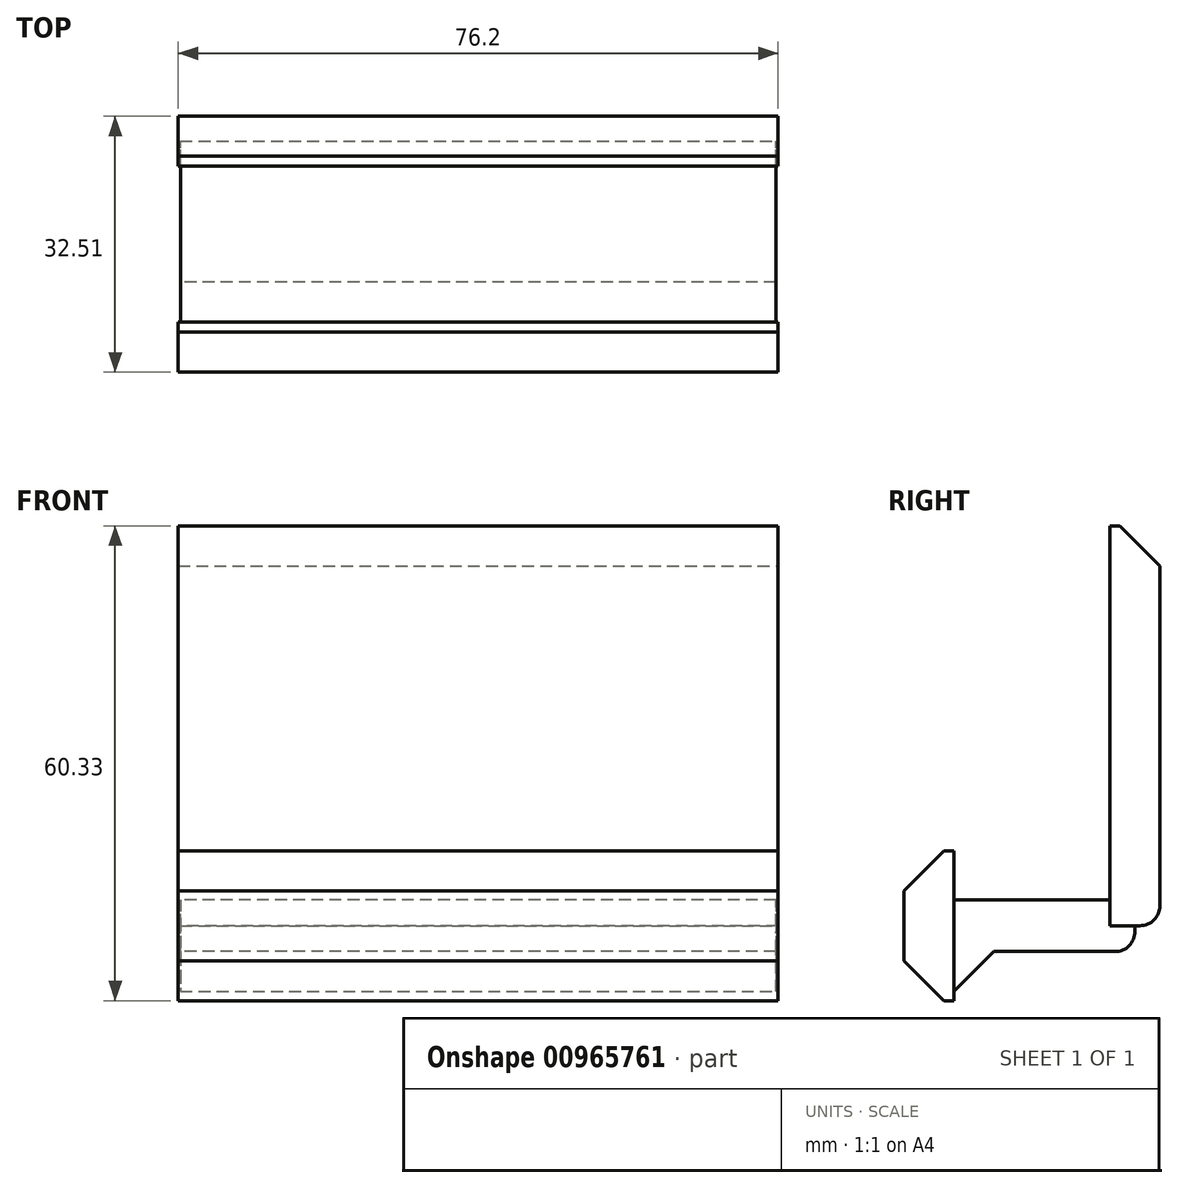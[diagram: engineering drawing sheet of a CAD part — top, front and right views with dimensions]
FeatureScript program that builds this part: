
annotation { "Feature Type Name" : "Feature", "Feature Type Description" : "" }
export const myFeature = defineFeature(function(context is Context, id is Id, definition is map)
    precondition{}
    {
        {
            var Q0;
            Q0=qCreatedBy(makeId("Top.planeOp"),FACE);
            var sketch = newSketch(context, id + "F0", { "sketchPlane" : qUnion([Q0])});
            skLineSegment(sketch, "E0.bottom", {"start": v(38.1, 3.18) * mm, "end": v(-38.1, 3.18) * mm});
            skLineSegment(sketch, "E0.top", {"start": v(38.1, -3.18) * mm, "end": v(-38.1, -3.18) * mm});
            skLineSegment(sketch, "E0.left", {"start": v(38.1, 3.18) * mm, "end": v(38.1, -3.18) * mm});
            skLineSegment(sketch, "E0.right", {"start": v(-38.1, 3.18) * mm, "end": v(-38.1, -3.18) * mm});
            skPoint(sketch, "E0.middle", {"position": v(0, 0) * mm});
            skSolve(sketch);
        }
        {
            var Q0;
            Q0=makeQuery(id+"F0.imprint","IMPRINT",FACE,{"disambiguationData":[TD([[makeQuery(id+"F0.imprint","IMPRINT",EDGE,{"derivedFrom":sQuery(id+"F0.wireOp",EDGE,"E0.bottom")}),1.0]])]});
            extrude(context, id + "F1", {"entities" : qUnion([Q0]), "depth" : 50.8 * mm, "offsetDistance" : 25.4 * mm});
        }
        {
            var Q0;
            Q0=qCreatedBy(makeId("Front.planeOp"),FACE);
            var sketch = newSketch(context, id + "F2", { "sketchPlane" : qUnion([Q0])});
            skLineSegment(sketch, "E1.bottom", {"start": v(37.8, 3.3) * mm, "end": v(-37.8, 3.3) * mm});
            skLineSegment(sketch, "E1.top", {"start": v(37.8, -3.3) * mm, "end": v(-37.8, -3.3) * mm});
            skLineSegment(sketch, "E1.left", {"start": v(37.8, 3.3) * mm, "end": v(37.8, -3.3) * mm});
            skLineSegment(sketch, "E1.right", {"start": v(-37.8, 3.3) * mm, "end": v(-37.8, -3.3) * mm});
            skPoint(sketch, "E1.middle", {"position": v(0, 0) * mm});
            skSolve(sketch);
        }
        {
            var Q0;
            Q0=makeQuery(id+"F2.imprint","IMPRINT",FACE,{"disambiguationData":[TD([[makeQuery(id+"F2.imprint","IMPRINT",EDGE,{"derivedFrom":sQuery(id+"F2.wireOp",EDGE,"E1.bottom")}),1.0]])]});
            extrude(context, id + "F3", {"entities" : qUnion([Q0]), "operationType" : NewBodyOperationType.ADD, "depth" : 25.4 * mm, "offsetDistance" : 25.4 * mm});
        }
        {
            var Q0;
            Q0=makeQuery(id+"F3.opExtrude","CAP_EDGE",EDGE,{"disambiguationData":[OSD([sQuery(id+"F2.wireOp",EDGE,"E1.top")])],"isStart":true});
            var Q1;
            Q1=makeQuery(id+"F1.opExtrude","CAP_EDGE",EDGE,{"disambiguationData":[OSD([sQuery(id+"F0.wireOp",EDGE,"E0.bottom")])],"isStart":true});
            fillet(context, id + "F4", {"entities" : qUnion([Q0, Q1]), "radius" : 2.54 * mm, "tangentPropagation" : true, "allowEdgeOverflow" : false});
        }
        {
            var Q0;
            Q0=makeQuery(id+"F1.opExtrude","CAP_EDGE",EDGE,{"disambiguationData":[OSD([sQuery(id+"F0.wireOp",EDGE,"E0.bottom")])],"isStart":false});
            chamfer(context, id + "F5", {"entities" : qUnion([Q0]), "width" : 5.08 * mm, "tangentPropagation" : true});
        }
        {
            var Q0;
            Q0=makeQuery(id+"F1.opExtrude","SWEPT_BODY",BODY,{"disambiguationData":[OSD([sQuery(id+"F0.wireOp",EDGE,"E0.bottom"),sQuery(id+"F0.wireOp",EDGE,"E0.top"),sQuery(id+"F0.wireOp",EDGE,"E0.left"),sQuery(id+"F0.wireOp",EDGE,"E0.right")])]});
            transform(context, id + "F6", {"entities" : qUnion([Q0]), "transformType" : TransformType.TRANSLATION_3D, "dx" : 0 * mm, "dy" : 26.16 * mm, "dz" : 0 * mm, "makeCopy" : false});
        }
        {
            var Q0;
            Q0 = qSketchRegion(id + "F0", true);
            extrude(context, id + "F7", {"entities" : qUnion([Q0]), "operationType" : NewBodyOperationType.ADD, "endBound" : BoundingType.SYMMETRIC, "depth" : 19.05 * mm, "offsetDistance" : 25.4 * mm});
        }
        {
            var Q0;
            Q0=makeQuery(id+"F1.opExtrude","SWEPT_BODY",BODY,{"disambiguationData":[OSD([sQuery(id+"F0.wireOp",EDGE,"E0.bottom"),sQuery(id+"F0.wireOp",EDGE,"E0.top"),sQuery(id+"F0.wireOp",EDGE,"E0.left"),sQuery(id+"F0.wireOp",EDGE,"E0.right")])]});
            transform(context, id + "F8", {"entities" : qUnion([Q0]), "transformType" : TransformType.TRANSLATION_3D, "dx" : 0 * mm, "dy" : -11.18 * mm, "dz" : 0 * mm, "makeCopy" : false});
        }
        {
            var Q0;
            Q0=makeQuery(id+"F7.boolean.opBoolean","INTERSECT",EDGE,{"derivedFrom":[makeQuery(id+"F3.opExtrude","SWEPT_FACE",FACE,{"disambiguationData":[OSD([sQuery(id+"F2.wireOp",EDGE,"E1.top")])]}),makeQuery(id+"F7.opExtrude","SWEPT_FACE",FACE,{"disambiguationData":[OSD([sQuery(id+"F0.wireOp",EDGE,"E0.bottom")])]})]});
            var Q1;
            Q1=makeQuery(id+"F7.opExtrude","CAP_EDGE",EDGE,{"disambiguationData":[OSD([sQuery(id+"F0.wireOp",EDGE,"E0.top")])],"isStart":true});
            var Q2;
            Q2=makeQuery(id+"F7.opExtrude","CAP_EDGE",EDGE,{"disambiguationData":[OSD([sQuery(id+"F0.wireOp",EDGE,"E0.top")])],"isStart":false});
            chamfer(context, id + "F9", {"entities" : qUnion([Q0, Q1, Q2]), "width" : 5.08 * mm, "tangentPropagation" : true});
        }
    });
